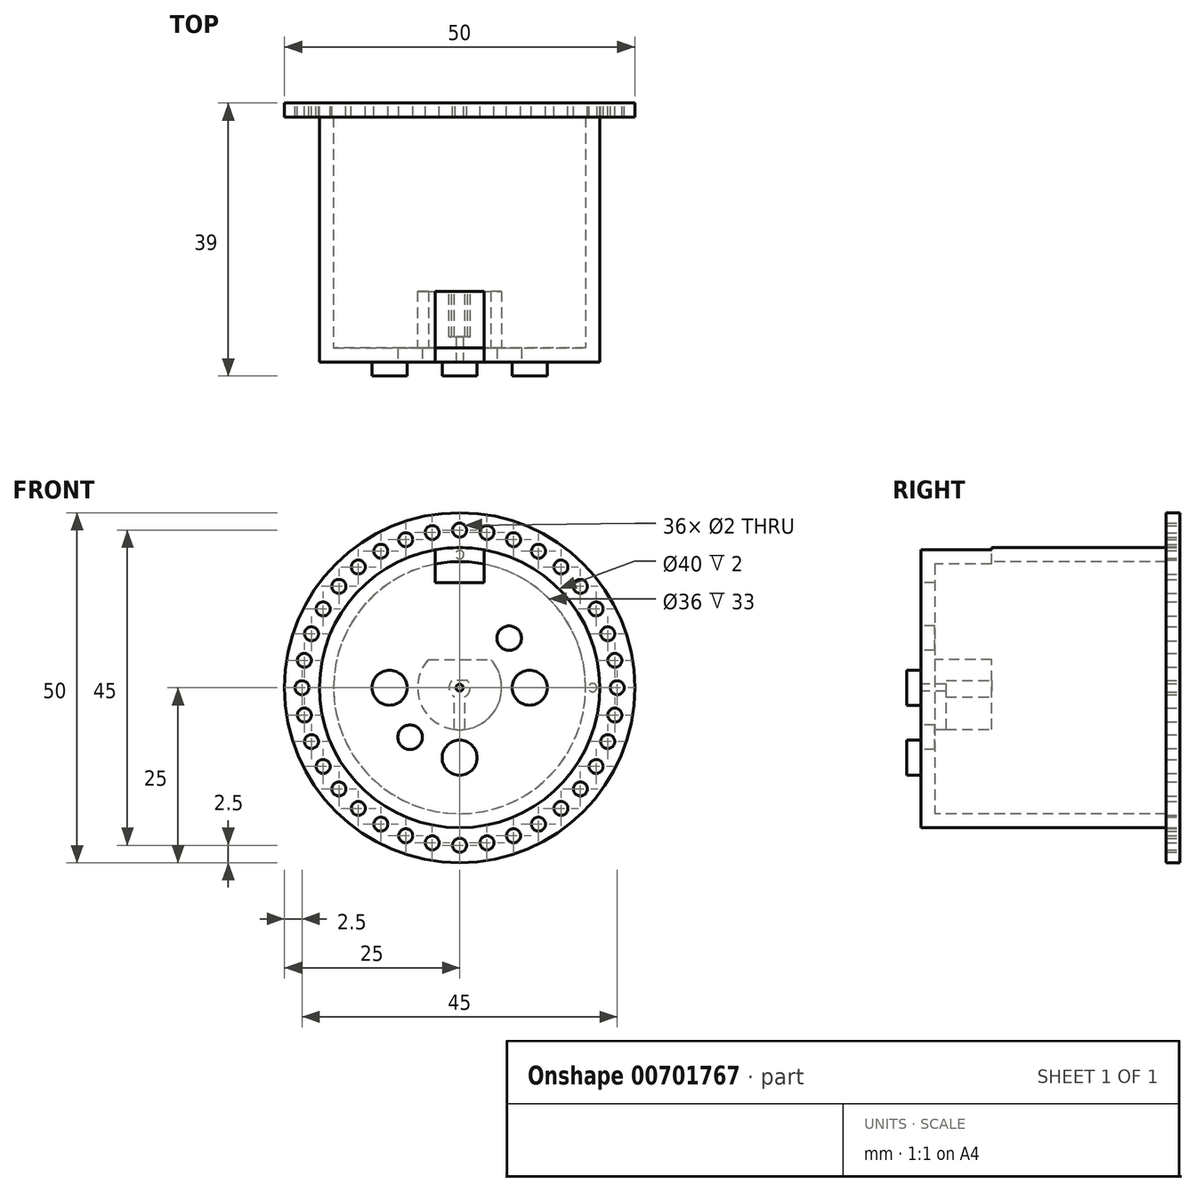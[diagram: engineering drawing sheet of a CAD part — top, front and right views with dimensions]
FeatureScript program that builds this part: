
annotation { "Feature Type Name" : "Feature", "Feature Type Description" : "" }
export const myFeature = defineFeature(function(context is Context, id is Id, definition is map)
    precondition{}
    {
        {
            var Q0;
            Q0=qCreatedBy(makeId("Front.planeOp"),FACE);
            var sketch = newSketch(context, id + "F0", { "sketchPlane" : qUnion([Q0])});
            skCircle(sketch, "E0", {"center": v(0, 0) * mm, "radius": 20 * mm});
            skCircle(sketch, "E1", {"center": v(0, 0) * mm, "radius": 6 * mm});
            skLineSegment(sketch, "E2", {"start": v(0, 0) * mm, "end": v(0, 20) * mm, "construction": true});
            skLineSegment(sketch, "E3.bottom", {"start": v(-3.5, 20) * mm, "end": v(3.5, 20) * mm});
            skLineSegment(sketch, "E3.top", {"start": v(-3.5, 15) * mm, "end": v(3.5, 15) * mm});
            skLineSegment(sketch, "E3.left", {"start": v(-3.5, 20) * mm, "end": v(-3.5, 15) * mm});
            skLineSegment(sketch, "E3.right", {"start": v(3.5, 20) * mm, "end": v(3.5, 15) * mm});
            skPoint(sketch, "E4", {"position": v(0, 15) * mm});
            skLineSegment(sketch, "E5", {"start": v(0, -20) * mm, "end": v(0, 0) * mm, "construction": true});
            skLineSegment(sketch, "E6", {"start": v(0, 0) * mm, "end": v(-20, 0) * mm, "construction": true});
            skLineSegment(sketch, "E7", {"start": v(0, 0) * mm, "end": v(20, 0) * mm, "construction": true});
            skPoint(sketch, "E8", {"position": v(-10, 0) * mm});
            skPoint(sketch, "E9", {"position": v(0, -10) * mm});
            skPoint(sketch, "E10", {"position": v(10, 0) * mm});
            skPoint(sketch, "E11", {"position": v(0, 10) * mm});
            skCircle(sketch, "E12", {"center": v(-10, 0) * mm, "radius": 2.5 * mm});
            skCircle(sketch, "E13", {"center": v(10, 0) * mm, "radius": 2.5 * mm});
            skCircle(sketch, "E14", {"center": v(0, -10) * mm, "radius": 2.5 * mm});
            skLineSegment(sketch, "E15", {"start": v(0, 0) * mm, "end": v(-20, -20) * mm, "construction": true});
            skLineSegment(sketch, "E16", {"start": v(0, 0) * mm, "end": v(20, 20) * mm, "construction": true});
            skLineSegment(sketch, "E17", {"start": v(0, 0) * mm, "end": v(20, -20) * mm, "construction": true});
            skLineSegment(sketch, "E18", {"start": v(0, 0) * mm, "end": v(-14.14, -14.14) * mm, "construction": true});
            skCircle(sketch, "E19", {"center": v(-7.07, -7.07) * mm, "radius": 1.75 * mm});
            skLineSegment(sketch, "E20", {"start": v(0, 0) * mm, "end": v(14.14, 14.14) * mm, "construction": true});
            skCircle(sketch, "E21", {"center": v(7.07, 7.07) * mm, "radius": 1.75 * mm});
            skLineSegment(sketch, "E22", {"start": v(-4.47, 4) * mm, "end": v(4.47, 4) * mm});
            skCircle(sketch, "E23", {"center": v(0, 0) * mm, "radius": 0.5 * mm});
            skSolve(sketch);
        }
        {
            var Q0;
            Q0=makeQuery(id+"F0.imprint","IMPRINT",FACE,{"disambiguationData":[TD([[makeQuery(id+"F0.imprint","IMPRINT",EDGE,{"derivedFrom":sQuery(id+"F0.wireOp",EDGE,"E1")}),-1.0]])]});
            var Q1;
            Q1=makeQuery(id+"F0.imprint","IMPRINT",FACE,{"disambiguationData":[TD([[makeQuery(id+"F0.imprint","IMPRINT",EDGE,{"derivedFrom":sQuery(id+"F0.wireOp",EDGE,"E1")}),1.0]])]});
            var Q2;
            {var subQ1=sQuery(id+"F0.wireOp",EDGE,"E3.top");Q2=makeQuery(id+"F0.imprint","IMPRINT",FACE,{"disambiguationData":[TD([[makeQuery(id+"F0.imprint","IMPRINT",EDGE,{"derivedFrom":subQ1}),1.0]])]});}
            var Q3;
            {var subQ0=sQuery(id+"F0.wireOp",EDGE,"Ytkhx9iy-BOv9-2ljm-Vuet-2ZozW4X65qVo.right");Q3=makeQuery(id+"F0.imprint","IMPRINT",FACE,{"disambiguationData":[TD([[makeQuery(id+"F0.imprint","IMPRINT",EDGE,{"derivedFrom":subQ0}),-1.0]])]});}
            var Q4;
            {var subQ0=sQuery(id+"F0.wireOp",EDGE,"KaZ6fn21-f6RE-yPpd-ZOH6-FnEf13cd3E14.left");Q4=makeQuery(id+"F0.imprint","IMPRINT",FACE,{"disambiguationData":[TD([[makeQuery(id+"F0.imprint","IMPRINT",EDGE,{"derivedFrom":subQ0}),1.0]])]});}
            var Q5;
            {var subQ1=sQuery(id+"F0.wireOp",EDGE,"QGJammbx-tseF-7Ff8-FYSq-d8eIJjrRkEd8.bottom");Q5=makeQuery(id+"F0.imprint","IMPRINT",FACE,{"disambiguationData":[TD([[makeQuery(id+"F0.imprint","IMPRINT",EDGE,{"derivedFrom":subQ1}),-1.0]])]});}
            var Q6;
            Q6=makeQuery(id+"F0.imprint","IMPRINT",FACE,{"disambiguationData":[TD([[makeQuery(id+"F0.imprint","IMPRINT",EDGE,{"derivedFrom":sQuery(id+"F0.wireOp",EDGE,"E12")}),1.0]])]});
            var Q7;
            Q7=makeQuery(id+"F0.imprint","IMPRINT",FACE,{"disambiguationData":[TD([[makeQuery(id+"F0.imprint","IMPRINT",EDGE,{"derivedFrom":sQuery(id+"F0.wireOp",EDGE,"E19")}),1.0]])]});
            var Q8;
            Q8=makeQuery(id+"F0.imprint","IMPRINT",FACE,{"disambiguationData":[TD([[makeQuery(id+"F0.imprint","IMPRINT",EDGE,{"derivedFrom":sQuery(id+"F0.wireOp",EDGE,"E14")}),1.0]])]});
            var Q9;
            Q9=makeQuery(id+"F0.imprint","IMPRINT",FACE,{"disambiguationData":[TD([[makeQuery(id+"F0.imprint","IMPRINT",EDGE,{"derivedFrom":sQuery(id+"F0.wireOp",EDGE,"E13")}),1.0]])]});
            var Q10;
            Q10=makeQuery(id+"F0.imprint","IMPRINT",FACE,{"disambiguationData":[TD([[makeQuery(id+"F0.imprint","IMPRINT",EDGE,{"derivedFrom":sQuery(id+"F0.wireOp",EDGE,"E21")}),1.0]])]});
            var Q11;
            {var subQ0=sQuery(id+"F0.wireOp",EDGE,"E22");Q11=makeQuery(id+"F0.imprint","IMPRINT",FACE,{"disambiguationData":[TD([[makeQuery(id+"F0.imprint","IMPRINT",EDGE,{"derivedFrom":subQ0}),-1.0]])]});}
            var Q12;
            Q12=makeQuery(id+"F0.imprint","IMPRINT",FACE,{"disambiguationData":[TD([[makeQuery(id+"F0.imprint","IMPRINT",EDGE,{"derivedFrom":sQuery(id+"F0.wireOp",EDGE,"E23")}),1.0]])]});
            extrude(context, id + "F1", {"entities" : qUnion([Q0, Q1, Q2, Q3, Q4, Q5, Q6, Q7, Q8, Q9, Q10, Q11, Q12]), "oppositeDirection" : true, "depth" : 37 * mm});
        }
        {
            var Q0;
            Q0=makeQuery(id+"F1.opExtrude","CAP_FACE",FACE,{"disambiguationData":[OSD([sQuery(id+"F0.wireOp",EDGE,"E0"),sQuery(id+"F0.wireOp",EDGE,"E3.top"),sQuery(id+"F0.wireOp",EDGE,"E3.left"),sQuery(id+"F0.wireOp",EDGE,"E3.right")])],"isStart":false});
            var Q1;
            Q1=makeQuery(id+"F1.opExtrude","SWEPT_FACE",FACE,{"disambiguationData":[OSD([sQuery(id+"F0.wireOp",EDGE,"E19")])]});
            var Q2;
            Q2=makeQuery(id+"F1.opExtrude","SWEPT_FACE",FACE,{"disambiguationData":[OSD([sQuery(id+"F0.wireOp",EDGE,"E14")])]});
            var Q3;
            Q3=makeQuery(id+"F1.opExtrude","SWEPT_FACE",FACE,{"disambiguationData":[OSD([sQuery(id+"F0.wireOp",EDGE,"E21")])]});
            var Q4;
            Q4=makeQuery(id+"F1.opExtrude","SWEPT_FACE",FACE,{"disambiguationData":[OSD([sQuery(id+"F0.wireOp",EDGE,"E13")])]});
            var Q5;
            Q5=makeQuery(id+"F1.opExtrude","SWEPT_FACE",FACE,{"disambiguationData":[OSD([sQuery(id+"F0.wireOp",EDGE,"E12")])]});
            shell(context, id + "F2", {"entities" : qUnion([Q0, Q1, Q2, Q3, Q4, Q5]), "thickness" : 2 * mm});
        }
        {
            var Q0;
            Q0=makeQuery(id+"F1.opExtrude","CAP_FACE",FACE,{"disambiguationData":[OSD([sQuery(id+"F0.wireOp",EDGE,"E0")])],"isStart":false});
            var sketch = newSketch(context, id + "F3", { "sketchPlane" : qUnion([Q0])});
            skCircle(sketch, "E24", {"center": v(0, 0) * mm, "radius": 25 * mm});
            skCircle(sketch, "E25", {"center": v(-22.5, 0) * mm, "radius": 1 * mm});
            skCircle(sketch, "E26.1.0", {"center": v(-22.16, -3.9) * mm, "radius": 1 * mm});
            skCircle(sketch, "E26.2.0", {"center": v(-21.14, -7.7) * mm, "radius": 1 * mm});
            skCircle(sketch, "E26.3.0", {"center": v(-19.49, -11.25) * mm, "radius": 1 * mm});
            skCircle(sketch, "E26.4.0", {"center": v(-17.24, -14.46) * mm, "radius": 1 * mm});
            skCircle(sketch, "E26.5.0", {"center": v(-14.46, -17.24) * mm, "radius": 1 * mm});
            skCircle(sketch, "E26.6.0", {"center": v(-11.25, -19.49) * mm, "radius": 1 * mm});
            skCircle(sketch, "E26.7.0", {"center": v(-7.7, -21.14) * mm, "radius": 1 * mm});
            skCircle(sketch, "E26.8.0", {"center": v(-3.9, -22.16) * mm, "radius": 1 * mm});
            skCircle(sketch, "E26.9.0", {"center": v(0, -22.5) * mm, "radius": 1 * mm});
            skCircle(sketch, "E26.10.0", {"center": v(3.9, -22.16) * mm, "radius": 1 * mm});
            skCircle(sketch, "E26.11.0", {"center": v(7.7, -21.14) * mm, "radius": 1 * mm});
            skCircle(sketch, "E26.12.0", {"center": v(11.25, -19.49) * mm, "radius": 1 * mm});
            skCircle(sketch, "E26.13.0", {"center": v(14.46, -17.24) * mm, "radius": 1 * mm});
            skCircle(sketch, "E26.14.0", {"center": v(17.24, -14.46) * mm, "radius": 1 * mm});
            skCircle(sketch, "E26.15.0", {"center": v(19.49, -11.25) * mm, "radius": 1 * mm});
            skCircle(sketch, "E26.16.0", {"center": v(21.14, -7.7) * mm, "radius": 1 * mm});
            skCircle(sketch, "E26.17.0", {"center": v(22.16, -3.9) * mm, "radius": 1 * mm});
            skCircle(sketch, "E26.18.0", {"center": v(22.5, 0) * mm, "radius": 1 * mm});
            skCircle(sketch, "E26.19.0", {"center": v(22.16, 3.9) * mm, "radius": 1 * mm});
            skCircle(sketch, "E26.20.0", {"center": v(21.14, 7.7) * mm, "radius": 1 * mm});
            skCircle(sketch, "E26.21.0", {"center": v(19.49, 11.25) * mm, "radius": 1 * mm});
            skCircle(sketch, "E26.22.0", {"center": v(17.24, 14.46) * mm, "radius": 1 * mm});
            skCircle(sketch, "E26.23.0", {"center": v(14.46, 17.24) * mm, "radius": 1 * mm});
            skCircle(sketch, "E26.24.0", {"center": v(11.25, 19.49) * mm, "radius": 1 * mm});
            skCircle(sketch, "E26.25.0", {"center": v(7.7, 21.14) * mm, "radius": 1 * mm});
            skCircle(sketch, "E27.1.26.0", {"center": v(3.9, 22.16) * mm, "radius": 1 * mm});
            skCircle(sketch, "E27.1.27.0", {"center": v(0, 22.5) * mm, "radius": 1 * mm});
            skCircle(sketch, "E27.1.28.0", {"center": v(-3.9, 22.16) * mm, "radius": 1 * mm});
            skCircle(sketch, "E27.1.29.0", {"center": v(-7.7, 21.14) * mm, "radius": 1 * mm});
            skCircle(sketch, "E27.1.30.0", {"center": v(-11.25, 19.49) * mm, "radius": 1 * mm});
            skCircle(sketch, "E27.1.31.0", {"center": v(-14.46, 17.24) * mm, "radius": 1 * mm});
            skCircle(sketch, "E27.1.32.0", {"center": v(-17.24, 14.46) * mm, "radius": 1 * mm});
            skCircle(sketch, "E27.1.33.0", {"center": v(-19.49, 11.25) * mm, "radius": 1 * mm});
            skCircle(sketch, "E27.1.34.0", {"center": v(-21.14, 7.7) * mm, "radius": 1 * mm});
            skCircle(sketch, "E27.1.35.0", {"center": v(-22.16, 3.9) * mm, "radius": 1 * mm});
            skCircle(sketch, "E28", {"center": v(-19, 0) * mm, "radius": 0.6 * mm});
            skLineSegment(sketch, "E29", {"start": v(0, -20) * mm, "end": v(0, 20) * mm, "construction": true});
            skCircle(sketch, "E30", {"center": v(-31.42, 9.46) * mm, "radius": 0.75 * mm});
            skLineSegment(sketch, "E31", {"start": v(0, 0) * mm, "end": v(-17.24, 17.24) * mm, "construction": true});
            skCircle(sketch, "E32.MirrorC", {"center": v(0, 19) * mm, "radius": 0.6 * mm});
            skSolve(sketch);
        }
        {
            var Q0;
            Q0=makeQuery(id+"F3.imprint","IMPRINT",FACE,{"disambiguationData":[TD([[makeQuery(id+"F3.imprint","IMPRINT",EDGE,{"derivedFrom":sQuery(id+"F3.wireOp",EDGE,"E24")}),1.0]])]});
            extrude(context, id + "F4", {"entities" : qUnion([Q0]), "operationType" : NewBodyOperationType.ADD, "oppositeDirection" : true, "depth" : 2 * mm});
        }
        {
            var Q0;
            Q0=makeQuery(id+"F3.imprint","IMPRINT",FACE,{"disambiguationData":[TD([[makeQuery(id+"F3.imprint","IMPRINT",EDGE,{"derivedFrom":sQuery(id+"F3.wireOp",EDGE,"E28")}),1.0]])]});
            var Q1;
            Q1=makeQuery(id+"F3.imprint","IMPRINT",FACE,{"disambiguationData":[TD([[makeQuery(id+"F3.imprint","IMPRINT",EDGE,{"derivedFrom":sQuery(id+"F3.wireOp",EDGE,"E32.MirrorC")}),-1.0]])]});
            extrude(context, id + "F5", {"entities" : qUnion([Q0, Q1]), "operationType" : NewBodyOperationType.REMOVE, "oppositeDirection" : true, "depth" : 2 * mm});
        }
        {
            var Q0;
            {var subQ0=sQuery(id+"F0.wireOp",EDGE,"E22");Q0=makeQuery(id+"F0.imprint","IMPRINT",FACE,{"disambiguationData":[TD([[makeQuery(id+"F0.imprint","IMPRINT",EDGE,{"derivedFrom":subQ0}),-1.0]])]});}
            extrude(context, id + "F6", {"entities" : qUnion([Q0]), "operationType" : NewBodyOperationType.ADD, "oppositeDirection" : true, "depth" : 10.1 * mm});
        }
        {
            var Q0;
            {var subQ1=sQuery(id+"F0.wireOp",EDGE,"E3.top");Q0=makeQuery(id+"F0.imprint","IMPRINT",FACE,{"disambiguationData":[TD([[makeQuery(id+"F0.imprint","IMPRINT",EDGE,{"derivedFrom":subQ1}),1.0]])]});}
            var Q1;
            Q1=makeQuery(id+"F6.opExtrude","CAP_FACE",FACE,{"disambiguationData":[OSD([sQuery(id+"F0.wireOp",EDGE,"E1")])],"isStart":false});
            extrude(context, id + "F7", {"entities" : qUnion([Q0]), "operationType" : NewBodyOperationType.REMOVE, "endBound" : BoundingType.UP_TO_SURFACE, "oppositeDirection" : true, "endBoundEntityFace" : qUnion([Q1]), "depth" : 10 * mm});
        }
        {
            var Q0;
            Q0=makeQuery(id+"F6.opExtrude","CAP_FACE",FACE,{"disambiguationData":[OSD([sQuery(id+"F0.wireOp",EDGE,"E1")])],"isStart":false});
            var sketch = newSketch(context, id + "F8", { "sketchPlane" : qUnion([Q0])});
            skArc(sketch, "E33", {"start": v(-1.12, 1) * mm, "mid": v(0, -1.5) * mm, "end": v(1.12, 1) * mm});
            skLineSegment(sketch, "E34", {"start": v(-1.12, 1) * mm, "end": v(1.12, 1) * mm});
            skLineSegment(sketch, "E35", {"start": v(-4.47, 4) * mm, "end": v(4.47, 4) * mm});
            skLineSegment(sketch, "E36.bottom", {"start": v(-0.75, -6) * mm, "end": v(0.75, -6) * mm});
            skLineSegment(sketch, "E36.top", {"start": v(-0.75, 0) * mm, "end": v(0.75, 0) * mm});
            skLineSegment(sketch, "E36.left", {"start": v(-0.75, -6) * mm, "end": v(-0.75, 0) * mm});
            skLineSegment(sketch, "E36.right", {"start": v(0.75, -6) * mm, "end": v(0.75, 0) * mm});
            skPoint(sketch, "E37", {"position": v(0, -6) * mm});
            skSolve(sketch);
        }
        {
            var Q0;
            Q0=makeQuery(id+"F8.imprint","IMPRINT",FACE,{"disambiguationData":[TD([[makeQuery(id+"F8.imprint","IMPRINT",EDGE,{"derivedFrom":sQuery(id+"F8.wireOp",EDGE,"E33")}),1.0]])]});
            var Q1;
            {var subQ0=sQuery(id+"F8.wireOp",EDGE,"E36.left");var subQ3=sQuery(id+"F8.wireOp",EDGE,"E33");var subQ4=makeQuery(id+"F8.imprint","INTERSECT",VERTEX,{"derivedFrom":[subQ3,subQ0]});Q1=makeQuery(id+"F8.imprint","IMPRINT",FACE,{"disambiguationData":[TD([[makeQuery(id+"F8.imprint","IMPRINT",EDGE,{"disambiguationData":[TD([[subQ4,-1.0]])],"derivedFrom":subQ3}),1.0]])]});}
            var Q2;
            {var subQ2=sQuery(id+"F8.wireOp",EDGE,"E36.left");var subQ5=sQuery(id+"F8.wireOp",EDGE,"E33");var subQ8=makeQuery(id+"F8.imprint","INTERSECT",VERTEX,{"derivedFrom":[subQ5,subQ2]});Q2=makeQuery(id+"F8.imprint","IMPRINT",FACE,{"disambiguationData":[TD([[makeQuery(id+"F8.imprint","IMPRINT",EDGE,{"disambiguationData":[TD([[subQ8,-1.0]])],"derivedFrom":subQ5}),-1.0]])]});}
            var Q3;
            {var subQ0=sQuery(id+"F0.wireOp",EDGE,"E0");Q3=makeQuery(id+"FelEgGFwdY7wIB0_0.boolean.opBoolean","MERGE",FACE,{"derivedFrom":[makeQuery(id+"F1.opExtrude","CAP_FACE",FACE,{"disambiguationData":[OSD([subQ0])],"isStart":true}),makeQuery(id+"FelEgGFwdY7wIB0_0.opExtrude","CAP_FACE",FACE,{"disambiguationData":[OSD([subQ0,sQuery(id+"F0.wireOp",EDGE,"1R5r3tbG-fw4S-uLm3-zZHl-8xL3PTXGlcnv"),sQuery(id+"F0.wireOp",EDGE,"Sdw5IeWT-c1RX-m7VR-ipaU-qvMlsCHA44hO"),sQuery(id+"F0.wireOp",EDGE,"fded56d8-0642-4762-9e0a-157306a48c7e.1.0"),sQuery(id+"F0.wireOp",EDGE,"fded56d8-0642-4762-9e0a-157306a48c7e.2.0"),sQuery(id+"F0.wireOp",EDGE,"fded56d8-0642-4762-9e0a-157306a48c7e.3.0"),sQuery(id+"F0.wireOp",EDGE,"fded56d8-0642-4762-9e0a-157306a48c7e.4.0"),sQuery(id+"F0.wireOp",EDGE,"fded56d8-0642-4762-9e0a-157306a48c7e.5.0"),sQuery(id+"F0.wireOp",EDGE,"fded56d8-0642-4762-9e0a-157306a48c7e.6.0"),sQuery(id+"F0.wireOp",EDGE,"fded56d8-0642-4762-9e0a-157306a48c7e.7.0"),sQuery(id+"F0.wireOp",EDGE,"fded56d8-0642-4762-9e0a-157306a48c7e.8.0"),sQuery(id+"F0.wireOp",EDGE,"fded56d8-0642-4762-9e0a-157306a48c7e.9.0"),sQuery(id+"F0.wireOp",EDGE,"fded56d8-0642-4762-9e0a-157306a48c7e.10.0"),sQuery(id+"F0.wireOp",EDGE,"fded56d8-0642-4762-9e0a-157306a48c7e.11.0"),sQuery(id+"F0.wireOp",EDGE,"fded56d8-0642-4762-9e0a-157306a48c7e.12.0"),sQuery(id+"F0.wireOp",EDGE,"fded56d8-0642-4762-9e0a-157306a48c7e.13.0"),sQuery(id+"F0.wireOp",EDGE,"fded56d8-0642-4762-9e0a-157306a48c7e.14.0"),sQuery(id+"F0.wireOp",EDGE,"fded56d8-0642-4762-9e0a-157306a48c7e.15.0"),sQuery(id+"F0.wireOp",EDGE,"fded56d8-0642-4762-9e0a-157306a48c7e.16.0"),sQuery(id+"F0.wireOp",EDGE,"fded56d8-0642-4762-9e0a-157306a48c7e.17.0"),sQuery(id+"F0.wireOp",EDGE,"fded56d8-0642-4762-9e0a-157306a48c7e.18.0"),sQuery(id+"F0.wireOp",EDGE,"fded56d8-0642-4762-9e0a-157306a48c7e.19.0"),sQuery(id+"F0.wireOp",EDGE,"fded56d8-0642-4762-9e0a-157306a48c7e.20.0"),sQuery(id+"F0.wireOp",EDGE,"fded56d8-0642-4762-9e0a-157306a48c7e.21.0"),sQuery(id+"F0.wireOp",EDGE,"fded56d8-0642-4762-9e0a-157306a48c7e.22.0"),sQuery(id+"F0.wireOp",EDGE,"fded56d8-0642-4762-9e0a-157306a48c7e.23.0"),sQuery(id+"F0.wireOp",EDGE,"fded56d8-0642-4762-9e0a-157306a48c7e.24.0"),sQuery(id+"F0.wireOp",EDGE,"fded56d8-0642-4762-9e0a-157306a48c7e.25.0")])],"isStart":true})]});}
            extrude(context, id + "F9", {"entities" : qUnion([Q0, Q1, Q2]), "operationType" : NewBodyOperationType.REMOVE, "oppositeDirection" : true, "endBoundEntityFace" : qUnion([Q3]), "depth" : 6.5 * mm});
        }
        {
            var Q0;
            Q0=makeQuery(id+"F3.imprint","IMPRINT",FACE,{"disambiguationData":[TD([[makeQuery(id+"F3.imprint","IMPRINT",EDGE,{"derivedFrom":sQuery(id+"F3.wireOp",EDGE,"E28")}),1.0]])]});
            extrude(context, id + "F10", {"entities" : qUnion([Q0]), "oppositeDirection" : true, "depth" : 2 * mm});
        }
        {
            var Q0;
            Q0=makeQuery(id+"F0.imprint","IMPRINT",FACE,{"disambiguationData":[TD([[makeQuery(id+"F0.imprint","IMPRINT",EDGE,{"derivedFrom":sQuery(id+"F0.wireOp",EDGE,"E12")}),1.0]])]});
            var Q1;
            Q1=makeQuery(id+"F0.imprint","IMPRINT",FACE,{"disambiguationData":[TD([[makeQuery(id+"F0.imprint","IMPRINT",EDGE,{"derivedFrom":sQuery(id+"F0.wireOp",EDGE,"E14")}),1.0]])]});
            var Q2;
            Q2=makeQuery(id+"F0.imprint","IMPRINT",FACE,{"disambiguationData":[TD([[makeQuery(id+"F0.imprint","IMPRINT",EDGE,{"derivedFrom":sQuery(id+"F0.wireOp",EDGE,"E13")}),1.0]])]});
            extrude(context, id + "F11", {"entities" : qUnion([Q0, Q1, Q2]), "operationType" : NewBodyOperationType.ADD, "depth" : 2 * mm});
        }
        {
            var Q0;
            Q0=makeQuery(id+"F0.imprint","IMPRINT",FACE,{"disambiguationData":[TD([[makeQuery(id+"F0.imprint","IMPRINT",EDGE,{"derivedFrom":sQuery(id+"F0.wireOp",EDGE,"E19")}),1.0]])]});
            var Q1;
            Q1=makeQuery(id+"F0.imprint","IMPRINT",FACE,{"disambiguationData":[TD([[makeQuery(id+"F0.imprint","IMPRINT",EDGE,{"derivedFrom":sQuery(id+"F0.wireOp",EDGE,"E21")}),1.0]])]});
            extrude(context, id + "F12", {"entities" : qUnion([Q0, Q1]), "operationType" : NewBodyOperationType.REMOVE, "endBound" : BoundingType.UP_TO_NEXT, "oppositeDirection" : true, "depth" : 25 * mm});
        }
        {
            var Q0;
            Q0=makeQuery(id+"F0.imprint","IMPRINT",FACE,{"disambiguationData":[TD([[makeQuery(id+"F0.imprint","IMPRINT",EDGE,{"derivedFrom":sQuery(id+"F0.wireOp",EDGE,"E23")}),1.0]])]});
            extrude(context, id + "F13", {"entities" : qUnion([Q0]), "operationType" : NewBodyOperationType.REMOVE, "endBound" : BoundingType.UP_TO_NEXT, "oppositeDirection" : true, "depth" : 25 * mm});
        }
    });
